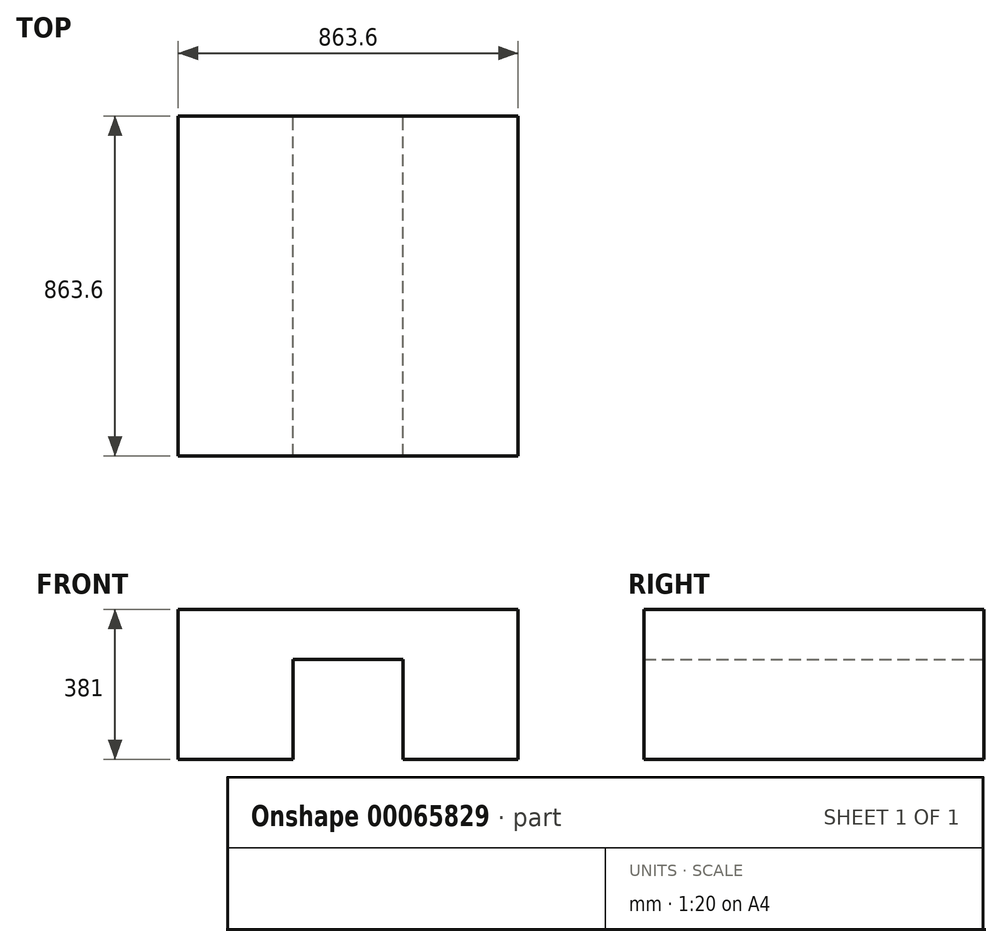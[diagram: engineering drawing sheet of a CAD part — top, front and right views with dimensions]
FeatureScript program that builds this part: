
annotation { "Feature Type Name" : "Feature", "Feature Type Description" : "" }
export const myFeature = defineFeature(function(context is Context, id is Id, definition is map)
    precondition{}
    {
        {
            var Q0;
            Q0=qCreatedBy(makeId("Front.planeOp"),FACE);
            var sketch = newSketch(context, id + "F0", { "sketchPlane" : qUnion([Q0])});
            skLineSegment(sketch, "E0.rect.bottom", {"start": v(-431.8, 381) * mm, "end": v(431.8, 381) * mm});
            skLineSegment(sketch, "E0.rect.top", {"start": v(-431.8, 0) * mm, "end": v(-139.7, 0) * mm});
            skLineSegment(sketch, "E0.rect.left", {"start": v(-431.8, 381) * mm, "end": v(-431.8, 0) * mm});
            skLineSegment(sketch, "E0.rect.right", {"start": v(431.8, 381) * mm, "end": v(431.8, 0) * mm});
            skLineSegment(sketch, "E1.trimOffspring", {"start": v(139.7, 0) * mm, "end": v(431.8, 0) * mm});
            skLineSegment(sketch, "E2.top", {"start": v(-139.7, 254) * mm, "end": v(139.7, 254) * mm});
            skLineSegment(sketch, "E2.left", {"start": v(-139.7, 0) * mm, "end": v(-139.7, 254) * mm});
            skLineSegment(sketch, "E2.right", {"start": v(139.7, 0) * mm, "end": v(139.7, 254) * mm});
            skSolve(sketch);
        }
        {
            var Q0;
            Q0=makeQuery(id+"F0.imprint","IMPRINT",FACE,{"disambiguationData":[TD([[makeQuery(id+"F0.imprint","IMPRINT",EDGE,{"derivedFrom":sQuery(id+"F0.wireOp",EDGE,"E0.rect.bottom")}),-1.0]])]});
            extrude(context, id + "F1", {"entities" : qUnion([Q0]), "depth" : 863.6 * mm});
        }
    });
